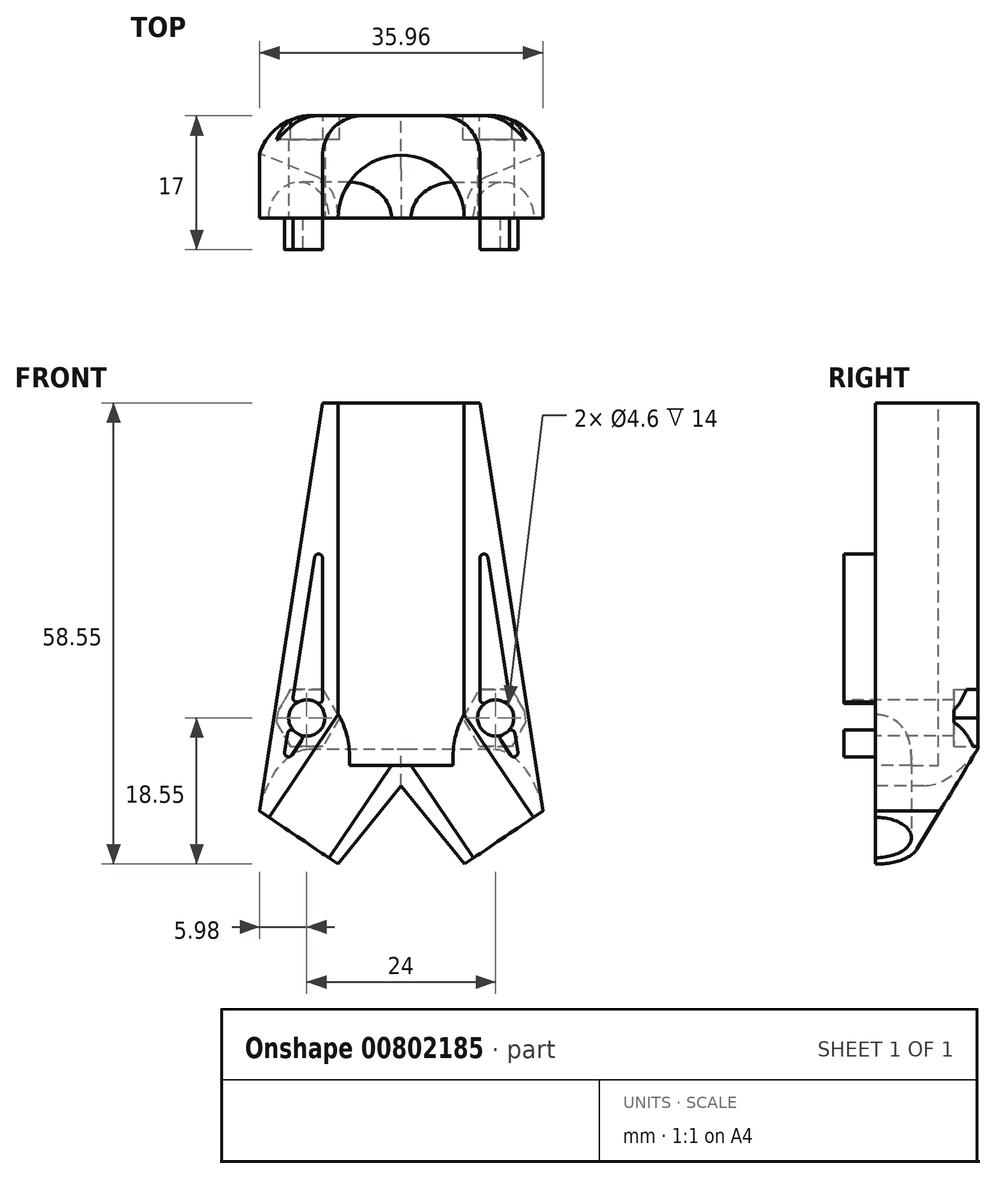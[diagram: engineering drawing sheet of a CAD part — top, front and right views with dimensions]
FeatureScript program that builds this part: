
annotation { "Feature Type Name" : "Feature", "Feature Type Description" : "" }
export const myFeature = defineFeature(function(context is Context, id is Id, definition is map)
    precondition{}
    {
        {
            var Q0;
            Q0=qCreatedBy(makeId("Front.planeOp"),FACE);
            var sketch = newSketch(context, id + "F0", { "sketchPlane" : qUnion([Q0])});
            skLineSegment(sketch, "E0", {"start": v(0, 0) * mm, "end": v(0, 0) * mm});
            skLineSegment(sketch, "E1.bottom", {"start": v(-10, 40) * mm, "end": v(10, 40) * mm});
            skLineSegment(sketch, "E2", {"start": v(0, -8.61) * mm, "end": v(-8.04, -18.55) * mm});
            skLineSegment(sketch, "E3", {"start": v(-8.04, -18.55) * mm, "end": v(-17.98, -11.83) * mm});
            skLineSegment(sketch, "E4", {"start": v(0, 54.25) * mm, "end": v(0, -48.28) * mm, "construction": true});
            skLineSegment(sketch, "E5.MirrorCS", {"start": v(0, -8.61) * mm, "end": v(8.04, -18.55) * mm});
            skLineSegment(sketch, "E6.MirrorCS", {"start": v(8.04, -18.55) * mm, "end": v(17.98, -11.83) * mm});
            skLineSegment(sketch, "E7", {"start": v(-10, 40) * mm, "end": v(-17.98, -11.83) * mm});
            skLineSegment(sketch, "E8", {"start": v(10, 40) * mm, "end": v(17.98, -11.83) * mm});
            skPoint(sketch, "E9.MirrorCS.start.orphan", {"position": v(10, 0) * mm});
            skLineSegment(sketch, "E10", {"start": v(-10, 40) * mm, "end": v(-10, 0) * mm, "construction": true});
            skLineSegment(sketch, "E11", {"start": v(-10, 0) * mm, "end": v(-17.98, -11.83) * mm, "construction": true});
            skLineSegment(sketch, "E12", {"start": v(10, 40) * mm, "end": v(10, 0) * mm, "construction": true});
            skLineSegment(sketch, "E13", {"start": v(10, 0) * mm, "end": v(17.98, -11.83) * mm, "construction": true});
            skLineSegment(sketch, "E14", {"start": v(-10, 0) * mm, "end": v(10, 0) * mm, "construction": true});
            skCircle(sketch, "E15", {"center": v(-12, 0) * mm, "radius": 2.3 * mm});
            skCircle(sketch, "E16.MirrorC", {"center": v(12, 0) * mm, "radius": 2.3 * mm});
            skLineSegment(sketch, "E17", {"start": v(0, 0) * mm, "end": v(13, -15.2) * mm, "construction": true});
            skSolve(sketch);
        }
        {
            var Q0;
            Q0=makeQuery(id+"F0.imprint","IMPRINT",FACE,{"disambiguationData":[TD([[makeQuery(id+"F0.imprint","IMPRINT",EDGE,{"derivedFrom":sQuery(id+"F0.wireOp",EDGE,"E1.bottom")}),-1.0]])]});
            var Q1;
            Q1=makeQuery(id+"F0.imprint","IMPRINT",FACE,{"disambiguationData":[TD([[makeQuery(id+"F0.imprint","IMPRINT",EDGE,{"derivedFrom":sQuery(id+"F0.wireOp",EDGE,"E1.top")}),-1.0]])]});
            extrude(context, id + "F1", {"entities" : qUnion([Q0, Q1]), "oppositeDirection" : true, "depth" : 13 * mm, "offsetDistance" : 25 * mm});
        }
        {
            var Q0;
            Q0=makeQuery(id+"F1.opExtrude","SWEPT_FACE",FACE,{"disambiguationData":[OSD([sQuery(id+"F0.wireOp",EDGE,"E1.bottom")])]});
            var sketch = newSketch(context, id + "F2", { "sketchPlane" : qUnion([Q0])});
            skCircle(sketch, "E18", {"center": v(0, 0) * mm, "radius": 8 * mm});
            skSolve(sketch);
        }
        {
            var Q0;
            {var subQ0=sQuery(id+"F2.wireOp",EDGE,"E18");var subQ1=makeQuery(id+"F1.opExtrude","CAP_EDGE",EDGE,{"disambiguationData":[OSD([sQuery(id+"F0.wireOp",EDGE,"E1.bottom")])],"isStart":true});var subQ2=makeQuery(id+"F2.imprint","INTERSECT",VERTEX,{"disambiguationData":[OD(0.0)],"derivedFrom":[subQ1,subQ0]});Q0=makeQuery(id+"F2.imprint","IMPRINT",FACE,{"disambiguationData":[TD([[makeQuery(id+"F2.imprint","IMPRINT",EDGE,{"disambiguationData":[TD([[subQ2,1.0]])],"derivedFrom":subQ0}),1.0]])]});}
            extrude(context, id + "F3", {"entities" : qUnion([Q0]), "operationType" : NewBodyOperationType.REMOVE, "oppositeDirection" : true, "depth" : 46 * mm, "offsetDistance" : 25 * mm});
        }
        {
            var Q0;
            Q0=qCreatedBy(makeId("Right.planeOp"),FACE);
            cPlane(context, id + "F4", {"entities" : qUnion([Q0]), "cplaneType" : CPlaneType.OFFSET, "offset" : 25 * mm, "width" : 150 * mm, "height" : 150 * mm});
        }
        {
            var Q0;
            Q0=qCreatedBy(id+"F4.planeOp",FACE);
            var sketch = newSketch(context, id + "F5", { "sketchPlane" : qUnion([Q0])});
            skLineSegment(sketch, "E19", {"start": v(4.14, -18.55) * mm, "end": v(13, -18.55) * mm});
            skLineSegment(sketch, "E20", {"start": v(13, -3.95) * mm, "end": v(13, -18.55) * mm});
            skLineSegment(sketch, "E21", {"start": v(4.14, -18.55) * mm, "end": v(13, -3.95) * mm});
            skSolve(sketch);
        }
        {
            var Q0;
            Q0=qSketchRegion(id+"F5",true);
            extrude(context, id + "F6", {"entities" : qUnion([Q0]), "operationType" : NewBodyOperationType.REMOVE, "oppositeDirection" : true, "depth" : 52.2 * mm, "offsetDistance" : 25 * mm});
        }
        {
            var Q0;
            Q0=makeQuery(id+"F1.opExtrude","SWEPT_FACE",FACE,{"disambiguationData":[OSD([sQuery(id+"F0.wireOp",EDGE,"E3")])]});
            var sketch = newSketch(context, id + "F7", { "sketchPlane" : qUnion([Q0])});
            skCircle(sketch, "E22", {"center": v(-2.28, 0) * mm, "radius": 4.6 * mm});
            skSolve(sketch);
        }
        {
            var Q0;
            {var subQ0=sQuery(id+"F7.wireOp",EDGE,"E22");var subQ1=makeQuery(id+"F1.opExtrude","CAP_EDGE",EDGE,{"disambiguationData":[OSD([sQuery(id+"F0.wireOp",EDGE,"E3")])],"isStart":true});var subQ2=makeQuery(id+"F7.imprint","INTERSECT",VERTEX,{"disambiguationData":[OD(0.0)],"derivedFrom":[subQ1,subQ0]});Q0=makeQuery(id+"F7.imprint","IMPRINT",FACE,{"disambiguationData":[TD([[makeQuery(id+"F7.imprint","IMPRINT",EDGE,{"disambiguationData":[TD([[subQ2,1.0]])],"derivedFrom":subQ0}),1.0]])]});}
            extrude(context, id + "F8", {"entities" : qUnion([Q0]), "operationType" : NewBodyOperationType.REMOVE, "oppositeDirection" : true, "depth" : 25 * mm, "offsetDistance" : 25 * mm});
        }
        {
            var Q0;
            Q0=makeQuery(id+"F1.opExtrude","SWEPT_FACE",FACE,{"disambiguationData":[OSD([sQuery(id+"F0.wireOp",EDGE,"E6.MirrorCS")])]});
            var sketch = newSketch(context, id + "F9", { "sketchPlane" : qUnion([Q0])});
            skCircle(sketch, "E23", {"center": v(2.28, 0) * mm, "radius": 4.6 * mm});
            skSolve(sketch);
        }
        {
            var Q0;
            {var subQ0=sQuery(id+"F9.wireOp",EDGE,"E23");var subQ1=makeQuery(id+"F1.opExtrude","CAP_EDGE",EDGE,{"disambiguationData":[OSD([sQuery(id+"F0.wireOp",EDGE,"E6.MirrorCS")])],"isStart":true});var subQ2=makeQuery(id+"F9.imprint","INTERSECT",VERTEX,{"disambiguationData":[OD(0.0)],"derivedFrom":[subQ1,subQ0]});Q0=makeQuery(id+"F9.imprint","IMPRINT",FACE,{"disambiguationData":[TD([[makeQuery(id+"F9.imprint","IMPRINT",EDGE,{"disambiguationData":[TD([[subQ2,-1.0]])],"derivedFrom":subQ0}),1.0]])]});}
            extrude(context, id + "F10", {"entities" : qUnion([Q0]), "operationType" : NewBodyOperationType.REMOVE, "oppositeDirection" : true, "depth" : 25 * mm, "offsetDistance" : 25 * mm});
        }
        {
            var Q0;
            Q0=makeQuery(id+"F1.opExtrude","CAP_EDGE",EDGE,{"disambiguationData":[OSD([sQuery(id+"F0.wireOp",EDGE,"E7")])],"isStart":false});
            var Q1;
            Q1=makeQuery(id+"F1.opExtrude","CAP_EDGE",EDGE,{"disambiguationData":[OSD([sQuery(id+"F0.wireOp",EDGE,"E8")])],"isStart":false});
            var Q2;
            Q2=makeQuery(id+"F6.boolean.opBoolean","INTERSECT",EDGE,{"derivedFrom":[makeQuery(id+"F1.opExtrude","SWEPT_FACE",FACE,{"disambiguationData":[OSD([sQuery(id+"F0.wireOp",EDGE,"E2")])]}),makeQuery(id+"F6.opExtrude","SWEPT_FACE",FACE,{"disambiguationData":[OSD([sQuery(id+"F5.wireOp",EDGE,"E21")])]})]});
            var Q3;
            Q3=makeQuery(id+"F6.boolean.opBoolean","INTERSECT",EDGE,{"derivedFrom":[makeQuery(id+"F1.opExtrude","SWEPT_FACE",FACE,{"disambiguationData":[OSD([sQuery(id+"F0.wireOp",EDGE,"E5.MirrorCS")])]}),makeQuery(id+"F6.opExtrude","SWEPT_FACE",FACE,{"disambiguationData":[OSD([sQuery(id+"F5.wireOp",EDGE,"E21")])]})]});
            fillet(context, id + "F11", {"entities" : qUnion([Q0, Q1, Q2, Q3]), "radius" : 5 * mm, "tangentPropagation" : true, "allowEdgeOverflow" : false});
        }
        {
            var Q0;
            {var subQ0=sQuery(id+"F0.wireOp",EDGE,"E8");var subQ2=sQuery(id+"F0.wireOp",EDGE,"E6.MirrorCS");var subQ4=sQuery(id+"F0.wireOp",EDGE,"E16.MirrorC");var subQ6=sQuery(id+"F0.wireOp",EDGE,"E1.bottom");var subQ7=makeQuery(id+"F1.opExtrude","SWEPT_FACE",FACE,{"disambiguationData":[OSD([subQ6])]});var subQ10=sQuery(id+"F0.wireOp",EDGE,"E3");var subQ11=sQuery(id+"F0.wireOp",EDGE,"E2");var subQ12=sQuery(id+"F0.wireOp",EDGE,"E5.MirrorCS");Q0=makeQuery(id+"F10.boolean.opBoolean","SPLIT",FACE,{"disambiguationData":[TD([subQ7])],"derivedFrom":makeQuery(id+"F8.boolean.opBoolean","SPLIT",FACE,{"disambiguationData":[TD([makeQuery(id+"F1.opExtrude","SWEPT_FACE",FACE,{"disambiguationData":[OSD([subQ11])]})])],"derivedFrom":makeQuery(id+"F1.opExtrude","CAP_FACE",FACE,{"disambiguationData":[OSD([subQ6,subQ11,subQ10,subQ12,subQ2,sQuery(id+"F0.wireOp",EDGE,"E7"),subQ0,sQuery(id+"F0.wireOp",EDGE,"E15"),subQ4])],"isStart":true})})});}
            var sketch = newSketch(context, id + "F12", { "sketchPlane" : qUnion([Q0])});
            skLineSegment(sketch, "E24.0", {"start": v(10, 26.86) * mm, "end": v(15.15, -6.56) * mm});
            skLineSegment(sketch, "E24.1", {"start": v(10, 1.05) * mm, "end": v(10, 26.86) * mm});
            skLineSegment(sketch, "E24.2", {"start": v(10, 1.05) * mm, "end": v(15.15, -6.56) * mm});
            skSolve(sketch);
        }
        {
            var Q0;
            {var subQ0=sQuery(id+"F0.wireOp",EDGE,"E7");var subQ1=sQuery(id+"F0.wireOp",EDGE,"E15");var subQ2=sQuery(id+"F0.wireOp",EDGE,"E3");var subQ3=sQuery(id+"F0.wireOp",EDGE,"E1.bottom");Q0=makeQuery(id+"F8.boolean.opBoolean","SPLIT",FACE,{"disambiguationData":[TD([makeQuery(id+"F1.opExtrude","SWEPT_FACE",FACE,{"disambiguationData":[OSD([subQ0])]})])],"derivedFrom":makeQuery(id+"F1.opExtrude","CAP_FACE",FACE,{"disambiguationData":[OSD([subQ3,sQuery(id+"F0.wireOp",EDGE,"E2"),subQ2,sQuery(id+"F0.wireOp",EDGE,"E5.MirrorCS"),sQuery(id+"F0.wireOp",EDGE,"E6.MirrorCS"),subQ0,sQuery(id+"F0.wireOp",EDGE,"E8"),subQ1,sQuery(id+"F0.wireOp",EDGE,"E16.MirrorC")])],"isStart":true})});}
            var sketch = newSketch(context, id + "F13", { "sketchPlane" : qUnion([Q0])});
            skSolve(sketch);
        }
        {
            var Q0;
            {var subQ6=sQuery(id+"F0.wireOp",EDGE,"E7");Q0=makeQuery(id+"F13.imprint","IMPRINT",FACE,{"disambiguationData":[TD([[makeQuery(id+"F13.imprint","IMPRINT",EDGE,{"derivedFrom":makeQuery(id+"F1.opExtrude","CAP_EDGE",EDGE,{"disambiguationData":[OSD([subQ6])],"isStart":true})}),1.0]])]});}
            var sketch = newSketch(context, id + "F14", { "sketchPlane" : qUnion([Q0])});
            skLineSegment(sketch, "E25.0", {"start": v(-10, 1.05) * mm, "end": v(-10, 26.86) * mm});
            skLineSegment(sketch, "E25.1", {"start": v(-10, 1.05) * mm, "end": v(-15.15, -6.56) * mm});
            skLineSegment(sketch, "E25.2", {"start": v(-10, 26.86) * mm, "end": v(-15.15, -6.56) * mm});
            skSolve(sketch);
        }
        {
            var Q0;
            Q0=qSketchRegion(id+"F14",true);
            extrude(context, id + "F15", {"entities" : qUnion([Q0]), "operationType" : NewBodyOperationType.ADD, "depth" : 4 * mm, "offsetDistance" : 25 * mm});
        }
        {
            var Q0;
            Q0=qSketchRegion(id+"F12",true);
            extrude(context, id + "F16", {"entities" : qUnion([Q0]), "operationType" : NewBodyOperationType.ADD, "depth" : 4 * mm, "offsetDistance" : 25 * mm});
        }
        {
            var Q0;
            Q0=makeQuery(id+"F1.opExtrude","CAP_FACE",FACE,{"disambiguationData":[OSD([sQuery(id+"F0.wireOp",EDGE,"E1.bottom"),sQuery(id+"F0.wireOp",EDGE,"E2"),sQuery(id+"F0.wireOp",EDGE,"E3"),sQuery(id+"F0.wireOp",EDGE,"E5.MirrorCS"),sQuery(id+"F0.wireOp",EDGE,"E6.MirrorCS"),sQuery(id+"F0.wireOp",EDGE,"E7"),sQuery(id+"F0.wireOp",EDGE,"E8"),sQuery(id+"F0.wireOp",EDGE,"E15"),sQuery(id+"F0.wireOp",EDGE,"E16.MirrorC")])],"isStart":false});
            cPlane(context, id + "F17", {"entities" : qUnion([Q0]), "cplaneType" : CPlaneType.OFFSET, "offset" : 25 * mm, "width" : 150 * mm, "height" : 150 * mm});
        }
        {
            var Q0;
            Q0=qCreatedBy(id+"F17.planeOp",FACE);
            var sketch = newSketch(context, id + "F18", { "sketchPlane" : qUnion([Q0])});
            skCircle(sketch, "E26.cCircle", {"center": v(-12, 0) * mm, "radius": 3.6 * mm, "construction": true});
            skLineSegment(sketch, "E26.0", {"start": v(-14.08, 3.6) * mm, "end": v(-9.92, 3.6) * mm});
            skLineSegment(sketch, "E26.1", {"start": v(-9.92, 3.6) * mm, "end": v(-7.84, 0) * mm});
            skLineSegment(sketch, "E26.2", {"start": v(-7.84, 0) * mm, "end": v(-9.92, -3.6) * mm});
            skLineSegment(sketch, "E26.3", {"start": v(-9.92, -3.6) * mm, "end": v(-14.08, -3.6) * mm});
            skLineSegment(sketch, "E26.4", {"start": v(-14.08, -3.6) * mm, "end": v(-16.16, 0) * mm});
            skLineSegment(sketch, "E26.5", {"start": v(-16.16, 0) * mm, "end": v(-14.08, 3.6) * mm});
            skPoint(sketch, "E26.0.midPoint", {"position": v(-12, 3.6) * mm});
            skCircle(sketch, "E27.cCircle", {"center": v(12, 0) * mm, "radius": 3.6 * mm, "construction": true});
            skLineSegment(sketch, "E27.0", {"start": v(9.92, 3.6) * mm, "end": v(14.08, 3.6) * mm});
            skLineSegment(sketch, "E27.1", {"start": v(14.08, 3.6) * mm, "end": v(16.16, 0) * mm});
            skLineSegment(sketch, "E27.2", {"start": v(16.16, 0) * mm, "end": v(14.08, -3.6) * mm});
            skLineSegment(sketch, "E27.3", {"start": v(14.08, -3.6) * mm, "end": v(9.92, -3.6) * mm});
            skLineSegment(sketch, "E27.4", {"start": v(9.92, -3.6) * mm, "end": v(7.84, 0) * mm});
            skLineSegment(sketch, "E27.5", {"start": v(7.84, 0) * mm, "end": v(9.92, 3.6) * mm});
            skPoint(sketch, "E27.0.midPoint", {"position": v(12, 3.6) * mm});
            skSolve(sketch);
        }
        {
            var Q0;
            Q0=makeQuery(id+"F18.imprint","IMPRINT",FACE,{"disambiguationData":[TD([[makeQuery(id+"F18.imprint","IMPRINT",EDGE,{"derivedFrom":sQuery(id+"F18.wireOp",EDGE,"E26.0")}),-1.0]])]});
            var Q1;
            Q1=makeQuery(id+"F18.imprint","IMPRINT",FACE,{"disambiguationData":[TD([[makeQuery(id+"F18.imprint","IMPRINT",EDGE,{"derivedFrom":sQuery(id+"F18.wireOp",EDGE,"E27.0")}),-1.0]])]});
            extrude(context, id + "F19", {"entities" : qUnion([Q0, Q1]), "operationType" : NewBodyOperationType.REMOVE, "oppositeDirection" : true, "depth" : 28 * mm, "offsetDistance" : 25 * mm});
        }
        {
            var Q0;
            Q0=makeQuery(id+"F15.opExtrude","CAP_FACE",FACE,{"disambiguationData":[OSD([sQuery(id+"F14.wireOp",EDGE,"E25.0"),sQuery(id+"F14.wireOp",EDGE,"E25.1"),sQuery(id+"F14.wireOp",EDGE,"E25.2")])],"isStart":false});
            var sketch = newSketch(context, id + "F20", { "sketchPlane" : qUnion([Q0])});
            skCircle(sketch, "E28", {"center": v(12, 0) * mm, "radius": 2.3 * mm});
            skSolve(sketch);
        }
        {
            var Q0;
            Q0 = qSketchRegion(id + "F20", true);
            extrude(context, id + "F21", {"entities" : qUnion([Q0]), "operationType" : NewBodyOperationType.REMOVE, "oppositeDirection" : true, "depth" : 25 * mm, "offsetDistance" : 25 * mm});
        }
        {
            var Q0;
            Q0=makeQuery(id+"F15.opExtrude","CAP_FACE",FACE,{"disambiguationData":[OSD([sQuery(id+"F14.wireOp",EDGE,"E25.0"),sQuery(id+"F14.wireOp",EDGE,"E25.1"),sQuery(id+"F14.wireOp",EDGE,"E25.2")])],"isStart":false});
            var sketch = newSketch(context, id + "F22", { "sketchPlane" : qUnion([Q0])});
            skCircle(sketch, "E29", {"center": v(-12, 0) * mm, "radius": 2.3 * mm});
            skSolve(sketch);
        }
        {
            var Q0;
            Q0 = qSketchRegion(id + "F22", true);
            extrude(context, id + "F23", {"entities" : qUnion([Q0]), "operationType" : NewBodyOperationType.REMOVE, "oppositeDirection" : true, "depth" : 25 * mm, "offsetDistance" : 25 * mm});
        }
        {
            var Q0;
            Q0=makeQuery(id+"F15.opExtrude","SWEPT_EDGE",EDGE,{"disambiguationData":[OSD([sQuery(id+"F14.wireOp",EDGE,"E25.0"),sQuery(id+"F14.wireOp",EDGE,"E25.2")])]});
            var Q1;
            Q1=makeQuery(id+"F16.opExtrude","SWEPT_EDGE",EDGE,{"disambiguationData":[OSD([sQuery(id+"F12.wireOp",EDGE,"E24.0"),sQuery(id+"F12.wireOp",EDGE,"E24.1")])]});
            var Q2;
            Q2=makeQuery(id+"F15.opExtrude","SWEPT_EDGE",EDGE,{"disambiguationData":[OSD([sQuery(id+"F14.wireOp",EDGE,"E25.1"),sQuery(id+"F14.wireOp",EDGE,"E25.2")])]});
            var Q3;
            Q3=makeQuery(id+"F16.opExtrude","SWEPT_EDGE",EDGE,{"disambiguationData":[OSD([sQuery(id+"F12.wireOp",EDGE,"E24.0"),sQuery(id+"F12.wireOp",EDGE,"E24.2")])]});
            var Q4;
            Q4=makeQuery(id+"F23.boolean.opBoolean","INTERSECT",EDGE,{"derivedFrom":[makeQuery(id+"F15.opExtrude","SWEPT_FACE",FACE,{"disambiguationData":[OSD([sQuery(id+"F14.wireOp",EDGE,"E25.0")])]}),makeQuery(id+"F23.opExtrude","SWEPT_FACE",FACE,{"disambiguationData":[OSD([sQuery(id+"F22.wireOp",EDGE,"E29")])]})]});
            var Q5;
            Q5=makeQuery(id+"F23.boolean.opBoolean","INTERSECT",EDGE,{"disambiguationData":[OD(0.0)],"derivedFrom":[makeQuery(id+"F15.opExtrude","SWEPT_FACE",FACE,{"disambiguationData":[OSD([sQuery(id+"F14.wireOp",EDGE,"E25.2")])]}),makeQuery(id+"F23.opExtrude","SWEPT_FACE",FACE,{"disambiguationData":[OSD([sQuery(id+"F22.wireOp",EDGE,"E29")])]})]});
            var Q6;
            Q6=makeQuery(id+"F21.boolean.opBoolean","INTERSECT",EDGE,{"derivedFrom":[makeQuery(id+"F16.opExtrude","SWEPT_FACE",FACE,{"disambiguationData":[OSD([sQuery(id+"F12.wireOp",EDGE,"E24.1")])]}),makeQuery(id+"F21.opExtrude","SWEPT_FACE",FACE,{"disambiguationData":[OSD([sQuery(id+"F20.wireOp",EDGE,"E28")])]})]});
            var Q7;
            Q7=makeQuery(id+"F21.boolean.opBoolean","INTERSECT",EDGE,{"disambiguationData":[OD(0.0)],"derivedFrom":[makeQuery(id+"F16.opExtrude","SWEPT_FACE",FACE,{"disambiguationData":[OSD([sQuery(id+"F12.wireOp",EDGE,"E24.0")])]}),makeQuery(id+"F21.opExtrude","SWEPT_FACE",FACE,{"disambiguationData":[OSD([sQuery(id+"F20.wireOp",EDGE,"E28")])]})]});
            var Q8;
            Q8=makeQuery(id+"F21.boolean.opBoolean","INTERSECT",EDGE,{"disambiguationData":[OD(1.0)],"derivedFrom":[makeQuery(id+"F16.opExtrude","SWEPT_FACE",FACE,{"disambiguationData":[OSD([sQuery(id+"F12.wireOp",EDGE,"E24.0")])]}),makeQuery(id+"F21.opExtrude","SWEPT_FACE",FACE,{"disambiguationData":[OSD([sQuery(id+"F20.wireOp",EDGE,"E28")])]})]});
            var Q9;
            Q9=makeQuery(id+"F21.boolean.opBoolean","INTERSECT",EDGE,{"derivedFrom":[makeQuery(id+"F16.opExtrude","SWEPT_FACE",FACE,{"disambiguationData":[OSD([sQuery(id+"F12.wireOp",EDGE,"E24.2")])]}),makeQuery(id+"F21.opExtrude","SWEPT_FACE",FACE,{"disambiguationData":[OSD([sQuery(id+"F20.wireOp",EDGE,"E28")])]})]});
            var Q10;
            Q10=makeQuery(id+"F23.boolean.opBoolean","INTERSECT",EDGE,{"derivedFrom":[makeQuery(id+"F15.opExtrude","SWEPT_FACE",FACE,{"disambiguationData":[OSD([sQuery(id+"F14.wireOp",EDGE,"E25.1")])]}),makeQuery(id+"F23.opExtrude","SWEPT_FACE",FACE,{"disambiguationData":[OSD([sQuery(id+"F22.wireOp",EDGE,"E29")])]})]});
            var Q11;
            Q11=makeQuery(id+"F23.boolean.opBoolean","INTERSECT",EDGE,{"disambiguationData":[OD(1.0)],"derivedFrom":[makeQuery(id+"F15.opExtrude","SWEPT_FACE",FACE,{"disambiguationData":[OSD([sQuery(id+"F14.wireOp",EDGE,"E25.2")])]}),makeQuery(id+"F23.opExtrude","SWEPT_FACE",FACE,{"disambiguationData":[OSD([sQuery(id+"F22.wireOp",EDGE,"E29")])]})]});
            fillet(context, id + "F24", {"entities" : qUnion([Q0, Q1, Q2, Q3, Q4, Q5, Q6, Q7, Q8, Q9, Q10, Q11]), "radius" : .5 * mm, "tangentPropagation" : true, "allowEdgeOverflow" : false});
        }
    });
